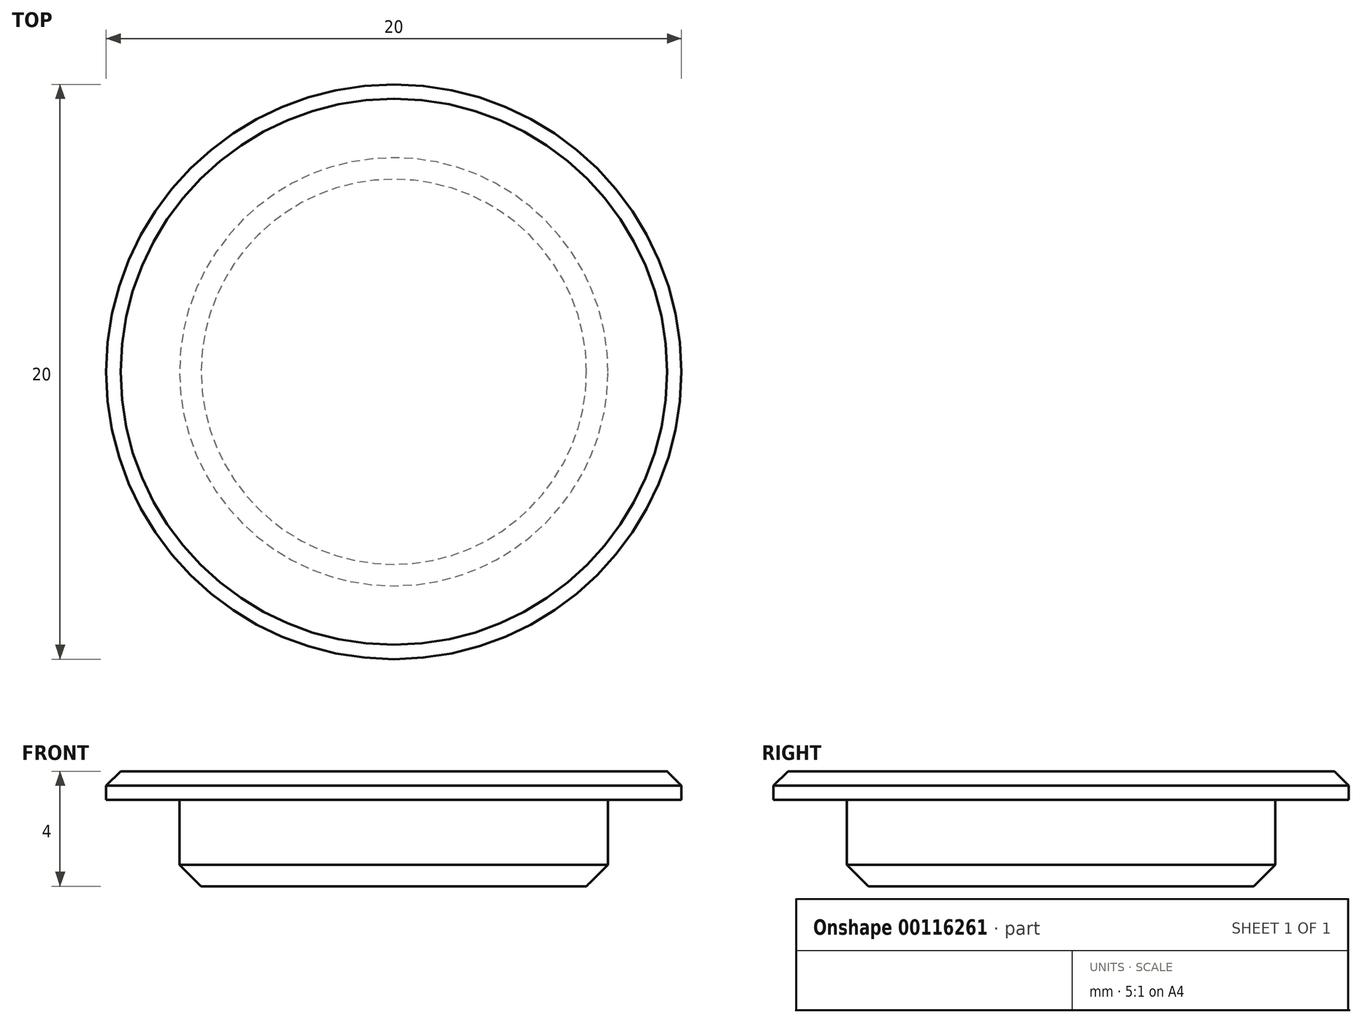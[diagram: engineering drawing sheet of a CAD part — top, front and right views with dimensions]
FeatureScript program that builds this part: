
annotation { "Feature Type Name" : "Feature", "Feature Type Description" : "" }
export const myFeature = defineFeature(function(context is Context, id is Id, definition is map)
    precondition{}
    {
        {
            var Q0;
            Q0=qCreatedBy(makeId("Top.planeOp"),FACE);
            var sketch = newSketch(context, id + "F0", { "sketchPlane" : qUnion([Q0])});
            skCircle(sketch, "E0", {"center": v(0, 0) * mm, "radius": 7.45 * mm});
            skSolve(sketch);
        }
        {
            var Q0;
            Q0 = qSketchRegion(id + "F0", true);
            extrude(context, id + "F1", {"entities" : qUnion([Q0]), "depth" : 3 * mm});
        }
        {
            var Q0;
            Q0=makeQuery(id+"F1.opExtrude","CAP_FACE",FACE,{"disambiguationData":[OSD([sQuery(id+"F0.wireOp",EDGE,"E0")])],"isStart":false});
            var sketch = newSketch(context, id + "F2", { "sketchPlane" : qUnion([Q0])});
            skPoint(sketch, "E1.0", {"position": v(0, 0) * mm});
            skCircle(sketch, "E2", {"center": v(0, 0) * mm, "radius": 10 * mm});
            skSolve(sketch);
        }
        {
            var Q0;
            Q0=makeQuery(id+"F2.imprint","IMPRINT",FACE,{"disambiguationData":[TD([[makeQuery(id+"F2.imprint","IMPRINT",EDGE,{"derivedFrom":makeQuery(id+"F1.opExtrude","CAP_EDGE",EDGE,{"disambiguationData":[OSD([sQuery(id+"F0.wireOp",EDGE,"E0")])],"isStart":false})}),1.0]])]});
            var Q1;
            Q1=makeQuery(id+"F2.imprint","IMPRINT",FACE,{"disambiguationData":[TD([[makeQuery(id+"F2.imprint","IMPRINT",EDGE,{"derivedFrom":sQuery(id+"F2.wireOp",EDGE,"E2")}),1.0]])]});
            extrude(context, id + "F3", {"entities" : qUnion([Q0, Q1]), "operationType" : NewBodyOperationType.ADD, "depth" : 1 * mm});
        }
        {
            var Q0;
            Q0=makeQuery(id+"F1.opExtrude","CAP_EDGE",EDGE,{"disambiguationData":[OSD([sQuery(id+"F0.wireOp",EDGE,"E0")])],"isStart":true});
            chamfer(context, id + "F4", {"entities" : qUnion([Q0]), "width" : 0.75 * mm, "tangentPropagation" : true});
        }
        {
            var Q0;
            Q0=makeQuery(id+"F3.opExtrude","CAP_EDGE",EDGE,{"disambiguationData":[OSD([sQuery(id+"F2.wireOp",EDGE,"E2")])],"isStart":false});
            chamfer(context, id + "F5", {"entities" : qUnion([Q0]), "width" : 0.5 * mm, "tangentPropagation" : true});
        }
    });
